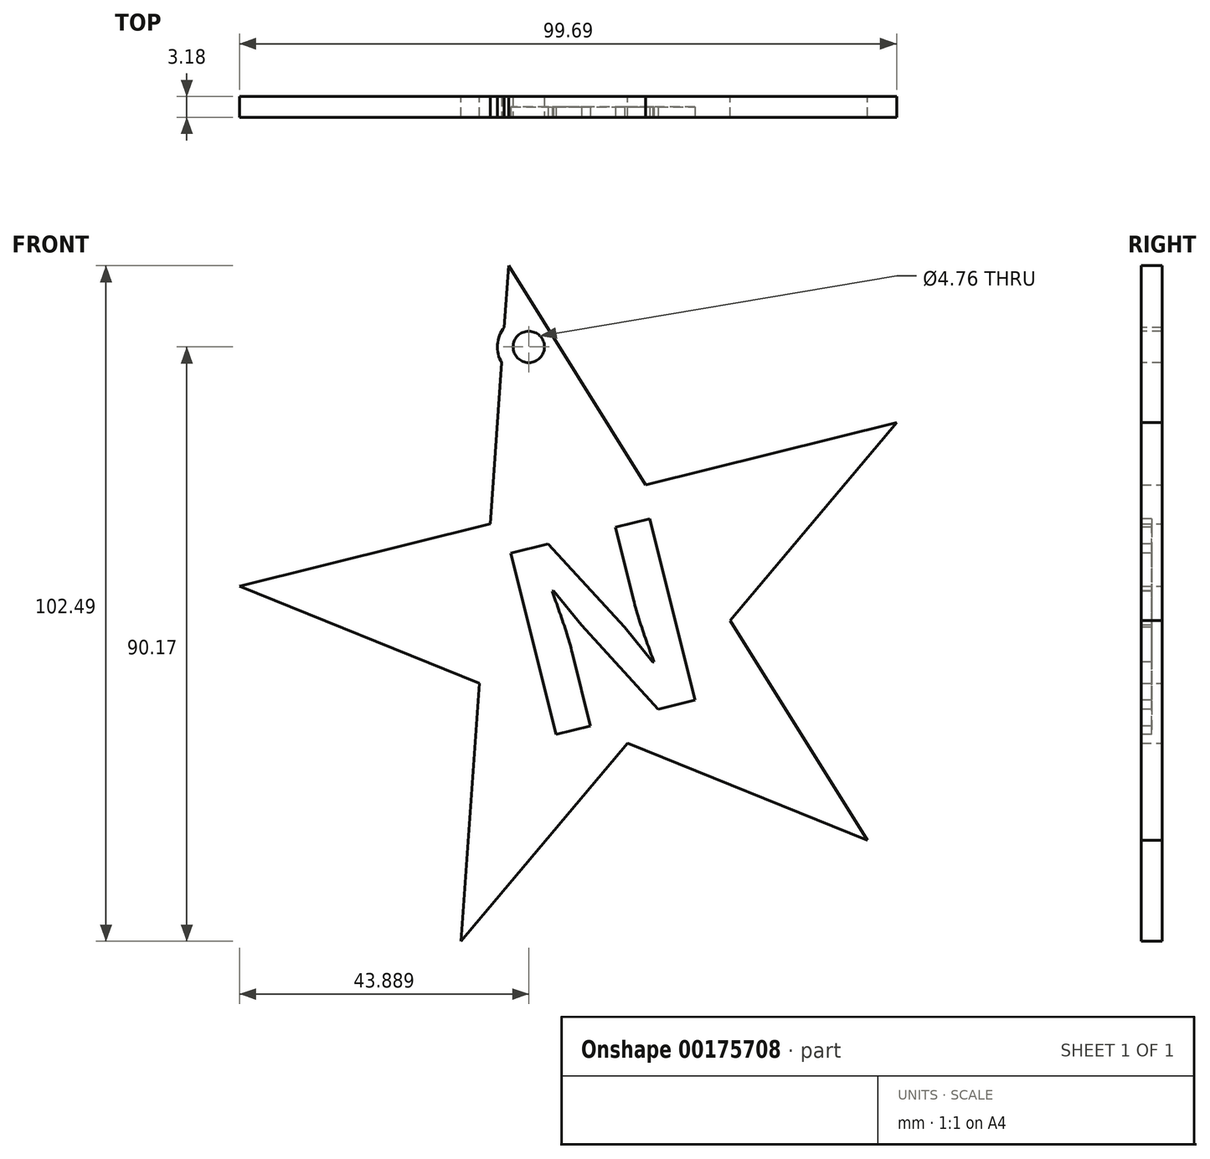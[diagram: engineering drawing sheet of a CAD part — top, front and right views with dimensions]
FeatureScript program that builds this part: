
annotation { "Feature Type Name" : "Feature", "Feature Type Description" : "" }
export const myFeature = defineFeature(function(context is Context, id is Id, definition is map)
    precondition{}
    {
        {
            var Q0;
            Q0=qCreatedBy(makeId("Front.planeOp"),FACE);
            var sketch = newSketch(context, id + "F0", { "sketchPlane" : qUnion([Q0])});
            skCircle(sketch, "E0.cCircle", {"center": v(0, 0) * mm, "radius": 43.7 * mm, "construction": true});
            skLineSegment(sketch, "E0.0", {"start": v(-13.06, 52.41) * mm, "end": v(45.81, 28.62) * mm});
            skLineSegment(sketch, "E0.1", {"start": v(45.81, 28.62) * mm, "end": v(41.37, -34.73) * mm});
            skLineSegment(sketch, "E0.2", {"start": v(41.37, -34.73) * mm, "end": v(-20.24, -50.08) * mm});
            skLineSegment(sketch, "E0.3", {"start": v(-20.24, -50.08) * mm, "end": v(-53.88, 3.77) * mm});
            skLineSegment(sketch, "E0.4", {"start": v(-53.88, 3.77) * mm, "end": v(-13.06, 52.41) * mm});
            skPoint(sketch, "E0.0.midPoint", {"position": v(16.38, 40.52) * mm});
            skLineSegment(sketch, "E1", {"start": v(-13.06, 52.41) * mm, "end": v(-20.24, -50.08) * mm});
            skLineSegment(sketch, "E2", {"start": v(-13.06, 52.41) * mm, "end": v(41.37, -34.73) * mm});
            skLineSegment(sketch, "E3", {"start": v(41.37, -34.73) * mm, "end": v(-53.88, 3.77) * mm});
            skLineSegment(sketch, "E4", {"start": v(-53.88, 3.77) * mm, "end": v(45.81, 28.62) * mm});
            skLineSegment(sketch, "E5", {"start": v(45.81, 28.62) * mm, "end": v(-20.24, -50.08) * mm});
            skSolve(sketch);
        }
        {
            var Q0;
            {var subQ1=sQuery(id+"F0.wireOp",EDGE,"E1");var subQ3=sQuery(id+"F0.wireOp",EDGE,"E4");var subQ4=makeQuery(id+"F0.imprint","INTERSECT",VERTEX,{"derivedFrom":[subQ1,subQ3]});Q0=makeQuery(id+"F0.imprint","IMPRINT",FACE,{"disambiguationData":[TD([[makeQuery(id+"F0.imprint","IMPRINT",EDGE,{"disambiguationData":[TD([[subQ4,-1.0]])],"derivedFrom":subQ3}),1.0]])]});}
            var Q1;
            {var subQ0=sQuery(id+"F0.wireOp",EDGE,"E4");var subQ1=sQuery(id+"F0.wireOp",EDGE,"E2");var subQ2=makeQuery(id+"F0.imprint","INTERSECT",VERTEX,{"derivedFrom":[subQ1,subQ0]});Q1=makeQuery(id+"F0.imprint","IMPRINT",FACE,{"disambiguationData":[TD([[makeQuery(id+"F0.imprint","IMPRINT",EDGE,{"disambiguationData":[TD([[subQ2,-1.0]])],"derivedFrom":subQ1}),1.0]])]});}
            var Q2;
            {var subQ0=sQuery(id+"F0.wireOp",EDGE,"E4");var subQ1=sQuery(id+"F0.wireOp",EDGE,"E1");var subQ2=makeQuery(id+"F0.imprint","INTERSECT",VERTEX,{"derivedFrom":[subQ1,subQ0]});Q2=makeQuery(id+"F0.imprint","IMPRINT",FACE,{"disambiguationData":[TD([[makeQuery(id+"F0.imprint","IMPRINT",EDGE,{"disambiguationData":[TD([[subQ2,-1.0]])],"derivedFrom":subQ1}),1.0]])]});}
            var Q3;
            {var subQ0=sQuery(id+"F0.wireOp",EDGE,"E4");var subQ1=sQuery(id+"F0.wireOp",EDGE,"E1");var subQ2=makeQuery(id+"F0.imprint","INTERSECT",VERTEX,{"derivedFrom":[subQ1,subQ0]});Q3=makeQuery(id+"F0.imprint","IMPRINT",FACE,{"disambiguationData":[TD([[makeQuery(id+"F0.imprint","IMPRINT",EDGE,{"disambiguationData":[TD([[subQ2,-1.0]])],"derivedFrom":subQ1}),-1.0]])]});}
            var Q4;
            {var subQ1=sQuery(id+"F0.wireOp",EDGE,"E1");var subQ3=sQuery(id+"F0.wireOp",EDGE,"E3");var subQ4=makeQuery(id+"F0.imprint","INTERSECT",VERTEX,{"derivedFrom":[subQ1,subQ3]});Q4=makeQuery(id+"F0.imprint","IMPRINT",FACE,{"disambiguationData":[TD([[makeQuery(id+"F0.imprint","IMPRINT",EDGE,{"disambiguationData":[TD([[subQ4,1.0]])],"derivedFrom":subQ3}),1.0]])]});}
            var Q5;
            {var subQ1=sQuery(id+"F0.wireOp",EDGE,"E2");var subQ3=sQuery(id+"F0.wireOp",EDGE,"E5");var subQ4=makeQuery(id+"F0.imprint","INTERSECT",VERTEX,{"derivedFrom":[subQ1,subQ3]});Q5=makeQuery(id+"F0.imprint","IMPRINT",FACE,{"disambiguationData":[TD([[makeQuery(id+"F0.imprint","IMPRINT",EDGE,{"disambiguationData":[TD([[subQ4,-1.0]])],"derivedFrom":subQ3}),1.0]])]});}
            extrude(context, id + "F1", {"entities" : qUnion([Q0, Q1, Q2, Q3, Q4, Q5]), "depth" : 3.17 * mm});
        }
        {
            var Q0;
            Q0=makeQuery(id+"F1.opExtrude","CAP_FACE",FACE,{"disambiguationData":[OSD([sQuery(id+"F0.wireOp",EDGE,"E1"),sQuery(id+"F0.wireOp",EDGE,"E2"),sQuery(id+"F0.wireOp",EDGE,"E3"),sQuery(id+"F0.wireOp",EDGE,"E4"),sQuery(id+"F0.wireOp",EDGE,"E5")])],"isStart":false});
            var sketch = newSketch(context, id + "F2", { "sketchPlane" : qUnion([Q0])});
            skText(sketch, "E6", { "text": "N", "fontName": "NotoSansCJKkr-Bold.otf"});
            skLineSegment(sketch, "E7", {"start": v(-15.8, 13.26) * mm, "end": v(7.73, 19.13) * mm});
            skLineSegment(sketch, "E8", {"start": v(-2.62, 10.5) * mm, "end": v(-4.04, 16.2) * mm});
            skPoint(sketch, "E8.endSnap0", {"position": v(-4.04, 16.2) * mm});
            const initialGuessF2  = {"E6": [-0.00921, -0.01955, 0.97032, 0.2418, 0.02758]};
            skSetInitialGuess(sketch, initialGuessF2);
            skSolve(sketch);
        }
        {
            var Q0;
            Q0=makeQuery(id+"F2.imprint","IMPRINT",FACE,{"disambiguationData":[TD([[makeQuery(id+"F2.imprint","IMPRINT",EDGE,{"derivedFrom":sQuery(id+"F2.wireOp",EDGE,"E6.sketch_text.stroke-0")}),1.0]])]});
            extrude(context, id + "F3", {"entities" : qUnion([Q0]), "operationType" : NewBodyOperationType.REMOVE, "oppositeDirection" : true, "depth" : 1.59 * mm});
        }
        {
            var Q0;
            Q0=makeQuery(id+"F1.opExtrude","CAP_FACE",FACE,{"disambiguationData":[OSD([sQuery(id+"F0.wireOp",EDGE,"E1"),sQuery(id+"F0.wireOp",EDGE,"E2"),sQuery(id+"F0.wireOp",EDGE,"E3"),sQuery(id+"F0.wireOp",EDGE,"E4"),sQuery(id+"F0.wireOp",EDGE,"E5")])],"isStart":false});
            var sketch = newSketch(context, id + "F4", { "sketchPlane" : qUnion([Q0])});
            skCircle(sketch, "E9", {"center": v(-10, 40.1) * mm, "radius": 2.38 * mm});
            skLineSegment(sketch, "E10", {"start": v(-15.8, 13.26) * mm, "end": v(7.73, 19.13) * mm});
            skLineSegment(sketch, "E11", {"start": v(-13.06, 52.41) * mm, "end": v(-4.04, 16.2) * mm});
            skCircle(sketch, "E12", {"center": v(-10, 40.1) * mm, "radius": 4.76 * mm});
            skSolve(sketch);
        }
        {
            var Q0;
            {var subQ0=sQuery(id+"F4.wireOp",EDGE,"E11");var subQ1=sQuery(id+"F4.wireOp",EDGE,"E9");var subQ2=makeQuery(id+"F4.imprint","INTERSECT",VERTEX,{"disambiguationData":[OD(0.0)],"derivedFrom":[subQ1,subQ0]});Q0=makeQuery(id+"F4.imprint","IMPRINT",FACE,{"disambiguationData":[TD([[makeQuery(id+"F4.imprint","IMPRINT",EDGE,{"disambiguationData":[TD([[subQ2,1.0]])],"derivedFrom":subQ1}),1.0]])]});}
            var Q1;
            {var subQ0=sQuery(id+"F4.wireOp",EDGE,"E11");var subQ1=sQuery(id+"F4.wireOp",EDGE,"E9");var subQ2=makeQuery(id+"F4.imprint","INTERSECT",VERTEX,{"disambiguationData":[OD(0.0)],"derivedFrom":[subQ1,subQ0]});Q1=makeQuery(id+"F4.imprint","IMPRINT",FACE,{"disambiguationData":[TD([[makeQuery(id+"F4.imprint","IMPRINT",EDGE,{"disambiguationData":[TD([[subQ2,-1.0]])],"derivedFrom":subQ1}),1.0]])]});}
            extrude(context, id + "F5", {"entities" : qUnion([Q0, Q1]), "operationType" : NewBodyOperationType.REMOVE, "oppositeDirection" : true, "depth" : 3.17 * mm});
        }
        {
            var Q0;
            {var subQ0=sQuery(id+"F4.wireOp",EDGE,"E12");var subQ1=sQuery(id+"F0.wireOp",EDGE,"E2");var subQ2=makeQuery(id+"F1.opExtrude","CAP_EDGE",EDGE,{"disambiguationData":[OSD([subQ1]),TDD([makeQuery(id+"F0.imprint","IMPRINT",EDGE,{"disambiguationData":[TD([[makeQuery(id+"F0.imprint","INTERSECT",VERTEX,{"derivedFrom":[subQ1,sQuery(id+"F0.wireOp",EDGE,"E4")]}),1.0]])],"derivedFrom":subQ1})])],"isStart":false});var subQ3=makeQuery(id+"F4.imprint","INTERSECT",VERTEX,{"disambiguationData":[OD(0.0)],"derivedFrom":[subQ2,subQ0]});Q0=makeQuery(id+"F4.imprint","IMPRINT",FACE,{"disambiguationData":[TD([[makeQuery(id+"F4.imprint","IMPRINT",EDGE,{"disambiguationData":[TD([[subQ3,1.0]])],"derivedFrom":subQ0}),1.0]])]});}
            var Q1;
            {var subQ0=sQuery(id+"F4.wireOp",EDGE,"E12");var subQ1=sQuery(id+"F0.wireOp",EDGE,"E1");var subQ2=makeQuery(id+"F1.opExtrude","CAP_EDGE",EDGE,{"disambiguationData":[OSD([subQ1]),TDD([makeQuery(id+"F0.imprint","IMPRINT",EDGE,{"disambiguationData":[TD([[makeQuery(id+"F0.imprint","INTERSECT",VERTEX,{"derivedFrom":[subQ1,sQuery(id+"F0.wireOp",EDGE,"E4")]}),1.0]])],"derivedFrom":subQ1})])],"isStart":false});var subQ3=makeQuery(id+"F4.imprint","INTERSECT",VERTEX,{"disambiguationData":[OD(0.0)],"derivedFrom":[subQ2,subQ0]});Q1=makeQuery(id+"F4.imprint","IMPRINT",FACE,{"disambiguationData":[TD([[makeQuery(id+"F4.imprint","IMPRINT",EDGE,{"disambiguationData":[TD([[subQ3,-1.0]])],"derivedFrom":subQ0}),1.0]])]});}
            extrude(context, id + "F6", {"entities" : qUnion([Q0, Q1]), "operationType" : NewBodyOperationType.ADD, "oppositeDirection" : true, "depth" : 3.17 * mm});
        }
    });
